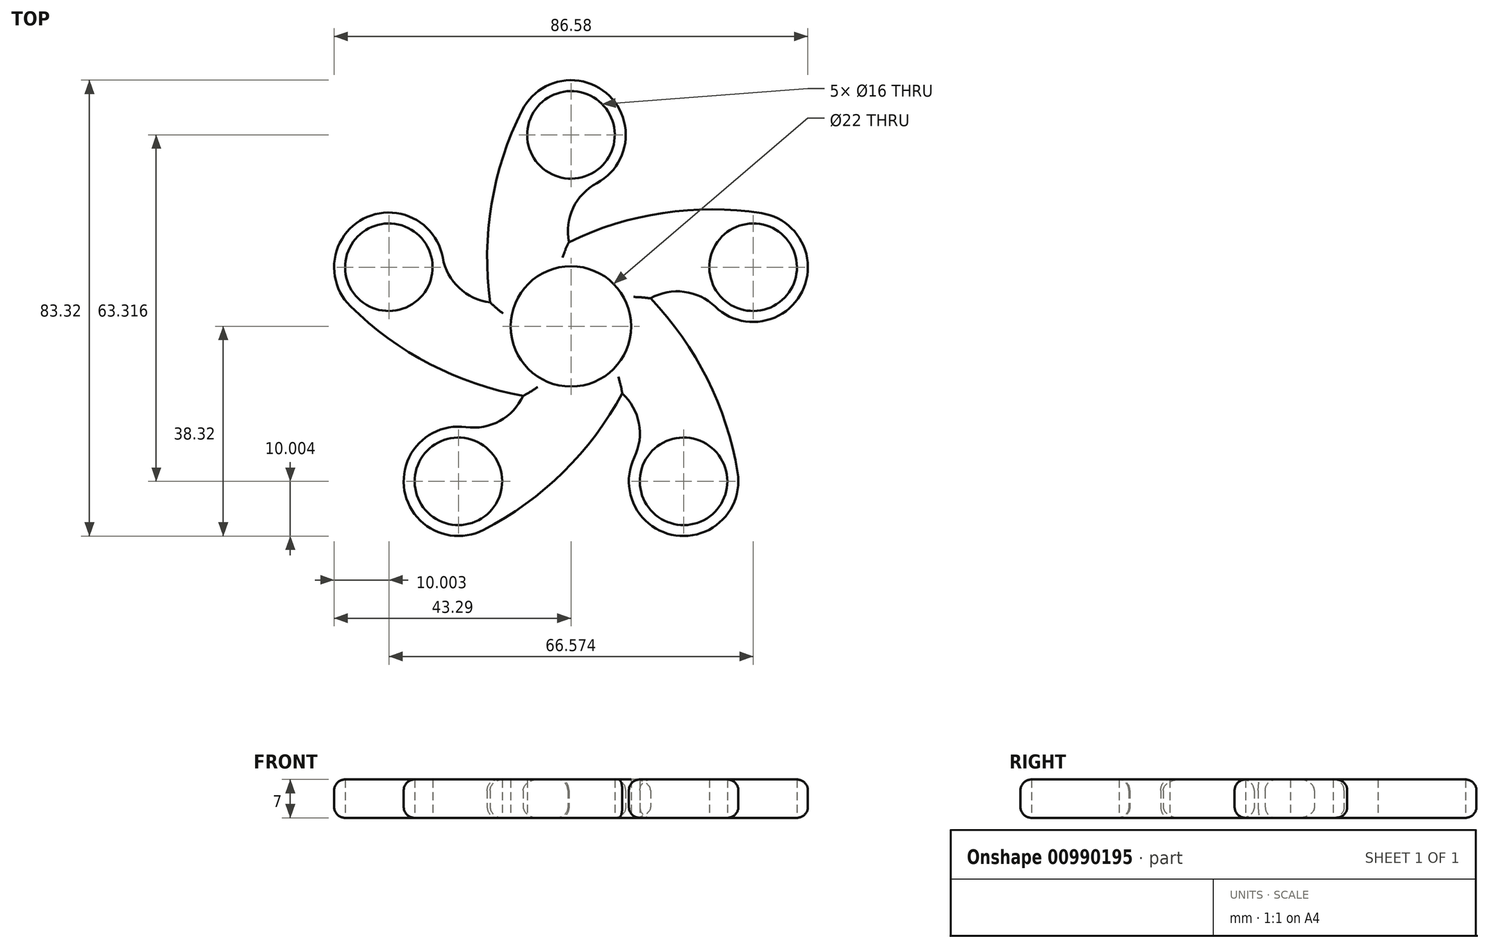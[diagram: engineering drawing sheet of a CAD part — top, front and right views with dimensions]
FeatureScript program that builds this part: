
annotation { "Feature Type Name" : "Feature", "Feature Type Description" : "" }
export const myFeature = defineFeature(function(context is Context, id is Id, definition is map)
    precondition{}
    {
        {
            assignVariable(context, id + "F0", {"name" : "number_of_arms", "anyValue" : 5});
        }
        {
            var Q0;
            Q0=qCreatedBy(makeId("Top.planeOp"),FACE);
            var sketch = newSketch(context, id + "F1", { "sketchPlane" : qUnion([Q0])});
            skCircle(sketch, "E0", {"center": v(0, 0) * mm, "radius": 11 * mm});
            skCircle(sketch, "E1", {"center": v(0, 0) * mm, "radius": 14 * mm});
            skCircle(sketch, "E2", {"center": v(0, 35) * mm, "radius": 8 * mm});
            skCircle(sketch, "E3", {"center": v(0, 35) * mm, "radius": 10 * mm});
            skArc(sketch, "E4", {"start": v(-8.93, 39.5) * mm, "mid": v(-14.84, 20.18) * mm, "end": v(-14, 0) * mm});
            skArc(sketch, "E5", {"start": v(4.7, 26.18) * mm, "mid": v(0.1, 20.96) * mm, "end": v(0, 14) * mm});
            skSolve(sketch);
        }
        {
            var Q0;
            Q0=qSketchRegion(id+"F1",true);
            extrude(context, id + "F2", {"entities" : qUnion([Q0]), "depth" : 7 * mm, "offsetDistance" : 25 * mm});
        }
        {
            var Q0;
            Q0=makeQuery(id+"F2.opExtrude","SWEPT_BODY",BODY,{"disambiguationData":[OSD([sQuery(id+"F1.wireOp",EDGE,"E0"),sQuery(id+"F1.wireOp",EDGE,"E1"),sQuery(id+"F1.wireOp",EDGE,"E2"),sQuery(id+"F1.wireOp",EDGE,"E3"),sQuery(id+"F1.wireOp",EDGE,"E4"),sQuery(id+"F1.wireOp",EDGE,"E5")])]});
            var Q1;
            Q1=makeQuery(id+"F2.opExtrude","CAP_EDGE",EDGE,{"disambiguationData":[OSD([sQuery(id+"F1.wireOp",EDGE,"E0")])],"isStart":false});
            circularPattern(context, id + "F3", {"operationType" : NewBodyOperationType.ADD, "entities" : qUnion([Q0]), "axis" : qUnion([Q1]), "angle" : 360 * degree, "instanceCount" : getVariable(context, 'number_of_arms'), "equalSpace" : true});
        }
        {
            var Q0;
            Q0=makeQuery(id+"F3.opPattern","COPY",EDGE,{"derivedFrom":makeQuery(id+"F2.opExtrude","CAP_EDGE",EDGE,{"disambiguationData":[OSD([sQuery(id+"F1.wireOp",EDGE,"E4")])],"isStart":false}),"instanceName":"3"});
            var Q1;
            Q1=makeQuery(id+"F3.opPattern","COPY",EDGE,{"derivedFrom":makeQuery(id+"F2.opExtrude","CAP_EDGE",EDGE,{"disambiguationData":[OSD([sQuery(id+"F1.wireOp",EDGE,"E3")])],"isStart":false}),"instanceName":"3"});
            var Q2;
            Q2=makeQuery(id+"F3.opPattern","COPY",EDGE,{"derivedFrom":makeQuery(id+"F2.opExtrude","CAP_EDGE",EDGE,{"disambiguationData":[OSD([sQuery(id+"F1.wireOp",EDGE,"E4")])],"isStart":false}),"instanceName":"2"});
            var Q3;
            Q3=makeQuery(id+"F3.opPattern","COPY",EDGE,{"derivedFrom":makeQuery(id+"F2.opExtrude","CAP_EDGE",EDGE,{"disambiguationData":[OSD([sQuery(id+"F1.wireOp",EDGE,"E4")])],"isStart":false}),"instanceName":"1"});
            var Q4;
            Q4=makeQuery(id+"F2.opExtrude","CAP_EDGE",EDGE,{"disambiguationData":[OSD([sQuery(id+"F1.wireOp",EDGE,"E4")])],"isStart":false});
            var Q5;
            Q5=makeQuery(id+"F3.opPattern","COPY",EDGE,{"derivedFrom":makeQuery(id+"F2.opExtrude","CAP_EDGE",EDGE,{"disambiguationData":[OSD([sQuery(id+"F1.wireOp",EDGE,"E4")])],"isStart":false}),"instanceName":"4"});
            var Q6;
            Q6=makeQuery(id+"F3.opPattern","COPY",EDGE,{"derivedFrom":makeQuery(id+"F2.opExtrude","CAP_EDGE",EDGE,{"disambiguationData":[OSD([sQuery(id+"F1.wireOp",EDGE,"E4")])],"isStart":true}),"instanceName":"3"});
            var Q7;
            Q7=makeQuery(id+"F2.opExtrude","CAP_EDGE",EDGE,{"disambiguationData":[OSD([sQuery(id+"F1.wireOp",EDGE,"E4")])],"isStart":true});
            var Q8;
            Q8=makeQuery(id+"F3.opPattern","COPY",EDGE,{"derivedFrom":makeQuery(id+"F2.opExtrude","CAP_EDGE",EDGE,{"disambiguationData":[OSD([sQuery(id+"F1.wireOp",EDGE,"E4")])],"isStart":true}),"instanceName":"1"});
            var Q9;
            Q9=makeQuery(id+"F3.opPattern","COPY",EDGE,{"derivedFrom":makeQuery(id+"F2.opExtrude","CAP_EDGE",EDGE,{"disambiguationData":[OSD([sQuery(id+"F1.wireOp",EDGE,"E4")])],"isStart":true}),"instanceName":"2"});
            var Q10;
            Q10=makeQuery(id+"F3.opPattern","COPY",EDGE,{"derivedFrom":makeQuery(id+"F2.opExtrude","CAP_EDGE",EDGE,{"disambiguationData":[OSD([sQuery(id+"F1.wireOp",EDGE,"E4")])],"isStart":true}),"instanceName":"4"});
            fillet(context, id + "F4", {"entities" : qUnion([Q0, Q1, Q2, Q3, Q4, Q5, Q6, Q7, Q8, Q9, Q10]), "radius" : 2 * mm, "tangentPropagation" : true, "allowEdgeOverflow" : false});
        }
    });
